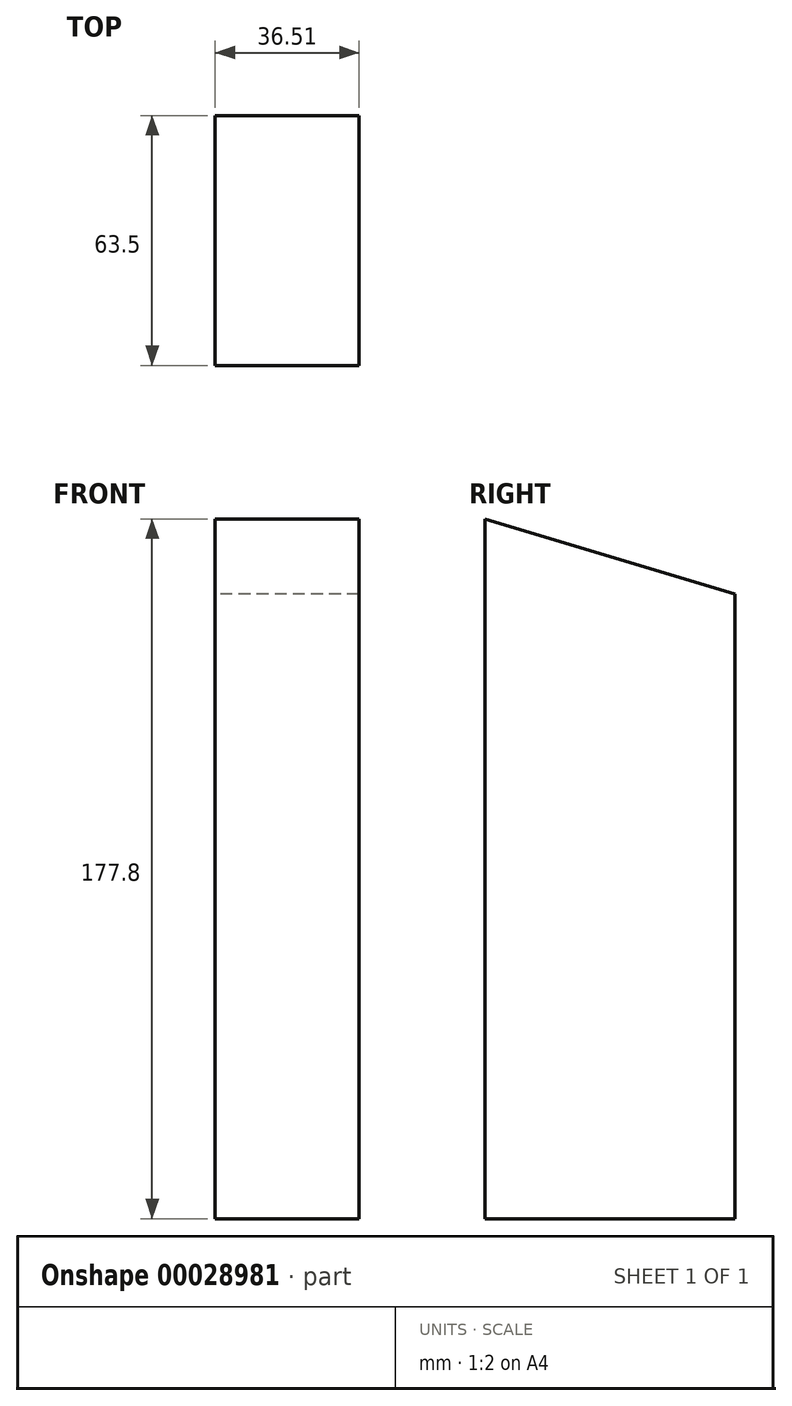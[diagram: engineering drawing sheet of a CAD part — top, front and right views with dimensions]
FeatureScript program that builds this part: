
annotation { "Feature Type Name" : "Feature", "Feature Type Description" : "" }
export const myFeature = defineFeature(function(context is Context, id is Id, definition is map)
    precondition{}
    {
        {
            var Q0;
            Q0=qCreatedBy(makeId("Right.planeOp"),FACE);
            var sketch = newSketch(context, id + "F0", { "sketchPlane" : qUnion([Q0])});
            skLineSegment(sketch, "E0", {"start": v(0, 0) * mm, "end": v(63.5, 0) * mm});
            skLineSegment(sketch, "E1", {"start": v(0, 0) * mm, "end": v(0, 177.8) * mm});
            skLineSegment(sketch, "E2", {"start": v(63.5, 0) * mm, "end": v(63.5, 158.75) * mm});
            skLineSegment(sketch, "E3", {"start": v(63.5, 158.75) * mm, "end": v(0, 177.8) * mm});
            skSolve(sketch);
        }
        {
            var Q0;
            Q0 = qSketchRegion(id + "F0", true);
            extrude(context, id + "F1", {"entities" : qUnion([Q0]), "depth" : 36.5 * mm});
        }
    });
